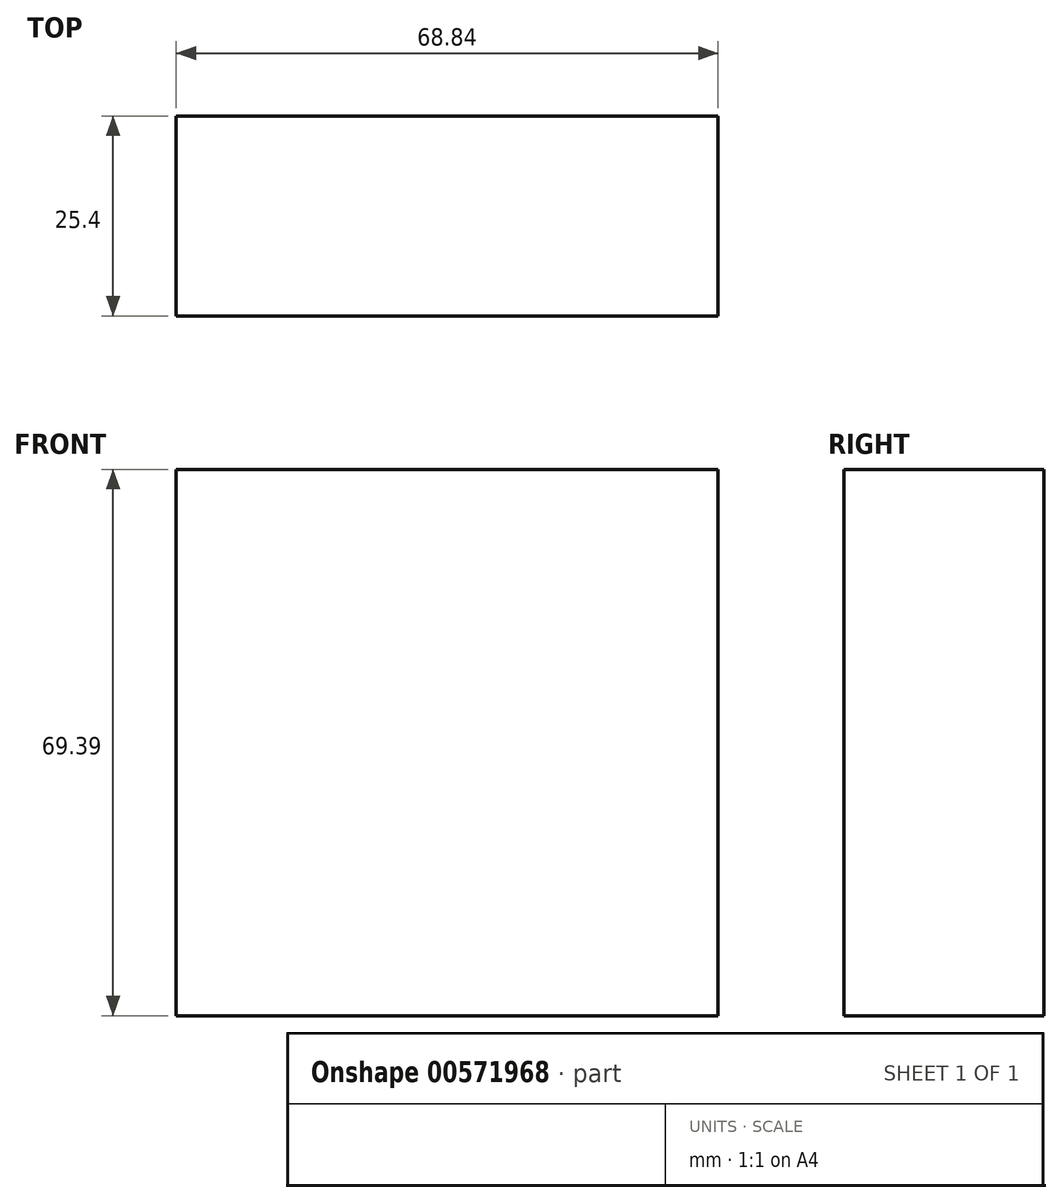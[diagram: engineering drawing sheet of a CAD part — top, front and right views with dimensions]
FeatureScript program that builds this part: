
annotation { "Feature Type Name" : "Feature", "Feature Type Description" : "" }
export const myFeature = defineFeature(function(context is Context, id is Id, definition is map)
    precondition{}
    {
        {
            var Q0;
            Q0=qCreatedBy(makeId("Front.planeOp"),FACE);
            var sketch = newSketch(context, id + "F0", { "sketchPlane" : qUnion([Q0])});
            skLineSegment(sketch, "E0.bottom", {"start": v(0, 0) * mm, "end": v(68.84, 0) * mm});
            skLineSegment(sketch, "E0.top", {"start": v(0, 69.39) * mm, "end": v(68.84, 69.39) * mm});
            skLineSegment(sketch, "E0.left", {"start": v(0, 0) * mm, "end": v(0, 69.39) * mm});
            skLineSegment(sketch, "E0.right", {"start": v(68.84, 0) * mm, "end": v(68.84, 69.39) * mm});
            skSolve(sketch);
        }
        {
            var Q0;
            Q0=makeQuery(id+"F0.imprint","IMPRINT",FACE,{"disambiguationData":[TD([[makeQuery(id+"F0.imprint","IMPRINT",EDGE,{"derivedFrom":sQuery(id+"F0.wireOp",EDGE,"E0.bottom")}),1.0]])]});
            extrude(context, id + "F1", {"entities" : qUnion([Q0]), "depth" : 25.4 * mm, "offsetDistance" : 25.4 * mm});
        }
    });
